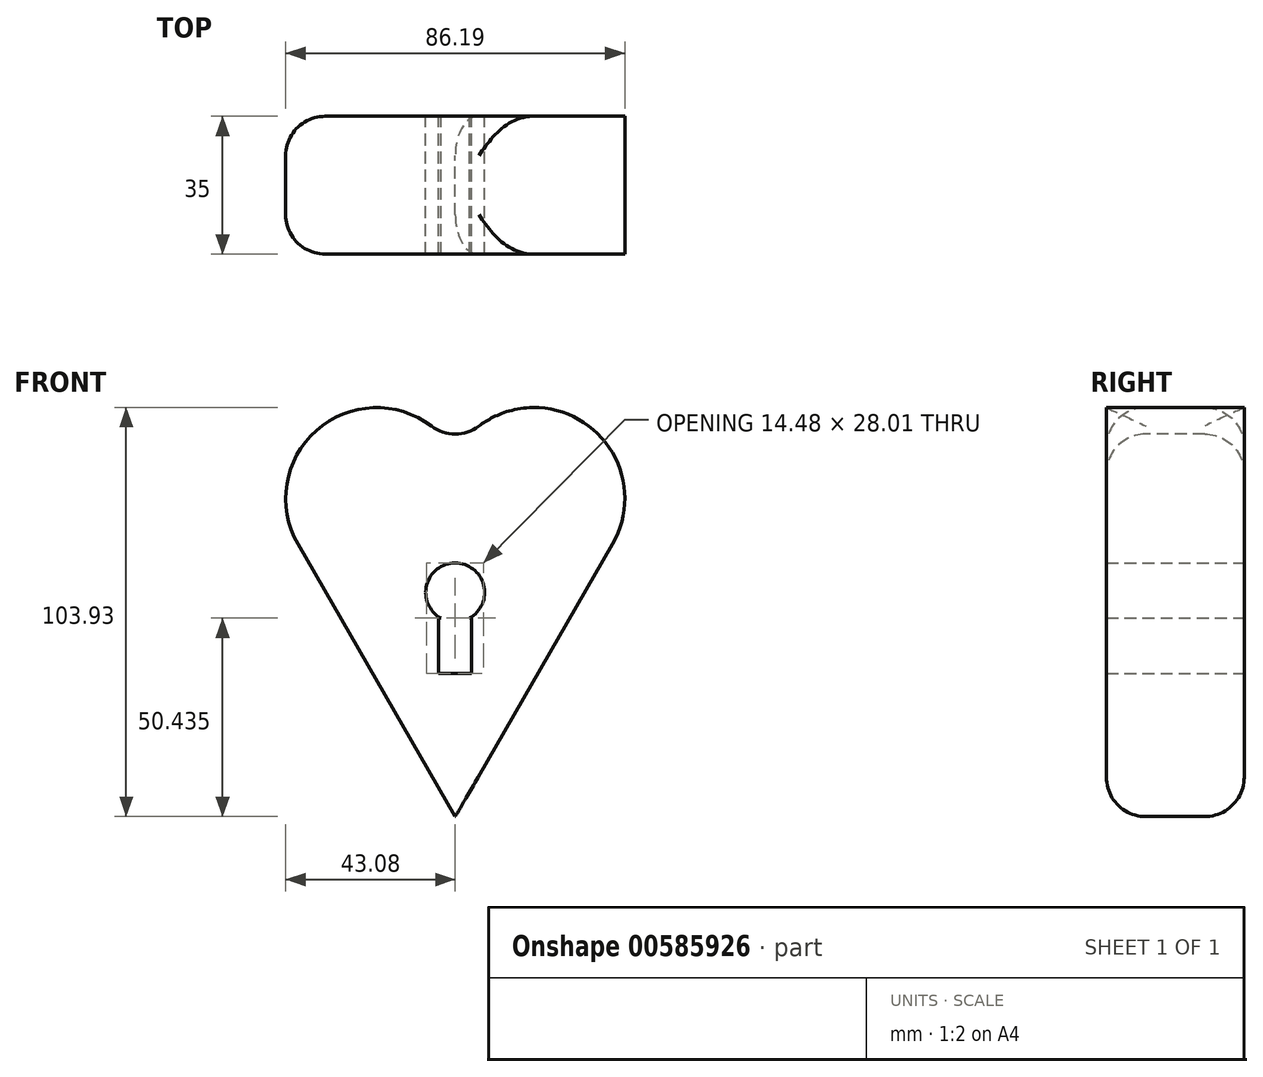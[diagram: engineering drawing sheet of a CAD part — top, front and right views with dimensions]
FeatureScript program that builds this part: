
annotation { "Feature Type Name" : "Feature", "Feature Type Description" : "" }
export const myFeature = defineFeature(function(context is Context, id is Id, definition is map)
    precondition{}
    {
        {
            var Q0;
            Q0=qCreatedBy(makeId("Front.planeOp"),FACE);
            var sketch = newSketch(context, id + "F0", { "sketchPlane" : qUnion([Q0])});
            skLineSegment(sketch, "E0", {"start": v(-39.99, 25.85) * mm, "end": v(0.01, -43.43) * mm});
            skLineSegment(sketch, "E1", {"start": v(0.01, -43.43) * mm, "end": v(40.01, 25.85) * mm});
            skArc(sketch, "E2", {"start": v(-39.99, 25.85) * mm, "mid": v(-20, 60.48) * mm, "end": v(0, 25.85) * mm});
            skArc(sketch, "E3", {"start": v(40.01, 25.85) * mm, "mid": v(20, 60.5) * mm, "end": v(0, 25.85) * mm});
            skCircle(sketch, "E4", {"center": v(0, 13.53) * mm, "radius": 7.48 * mm});
            skLineSegment(sketch, "E5.bottom", {"start": v(4.2, -7) * mm, "end": v(-4.2, -7) * mm});
            skLineSegment(sketch, "E5.top", {"start": v(4.2, 7) * mm, "end": v(-4.2, 7) * mm});
            skLineSegment(sketch, "E5.left", {"start": v(4.2, -7) * mm, "end": v(4.2, 7) * mm});
            skLineSegment(sketch, "E5.right", {"start": v(-4.2, -7) * mm, "end": v(-4.2, 7) * mm});
            skPoint(sketch, "E5.middle", {"position": v(0, 0) * mm});
            skSolve(sketch);
        }
        {
            var Q0;
            Q0 = qSketchRegion(id + "F0", true);
            extrude(context, id + "F1", {"entities" : qUnion([Q0]), "depth" : 35 * mm, "offsetDistance" : 25 * mm});
        }
        {
            var Q0;
            Q0=makeQuery(id+"F1.opExtrude","SWEPT_FACE",FACE,{"disambiguationData":[OSD([sQuery(id+"F0.wireOp",EDGE,"E2")])]});
            fillet(context, id + "F2", {"entities" : qUnion([Q0]), "radius" : 10 * mm, "tangentPropagation" : true, "allowEdgeOverflow" : false});
        }
    });
